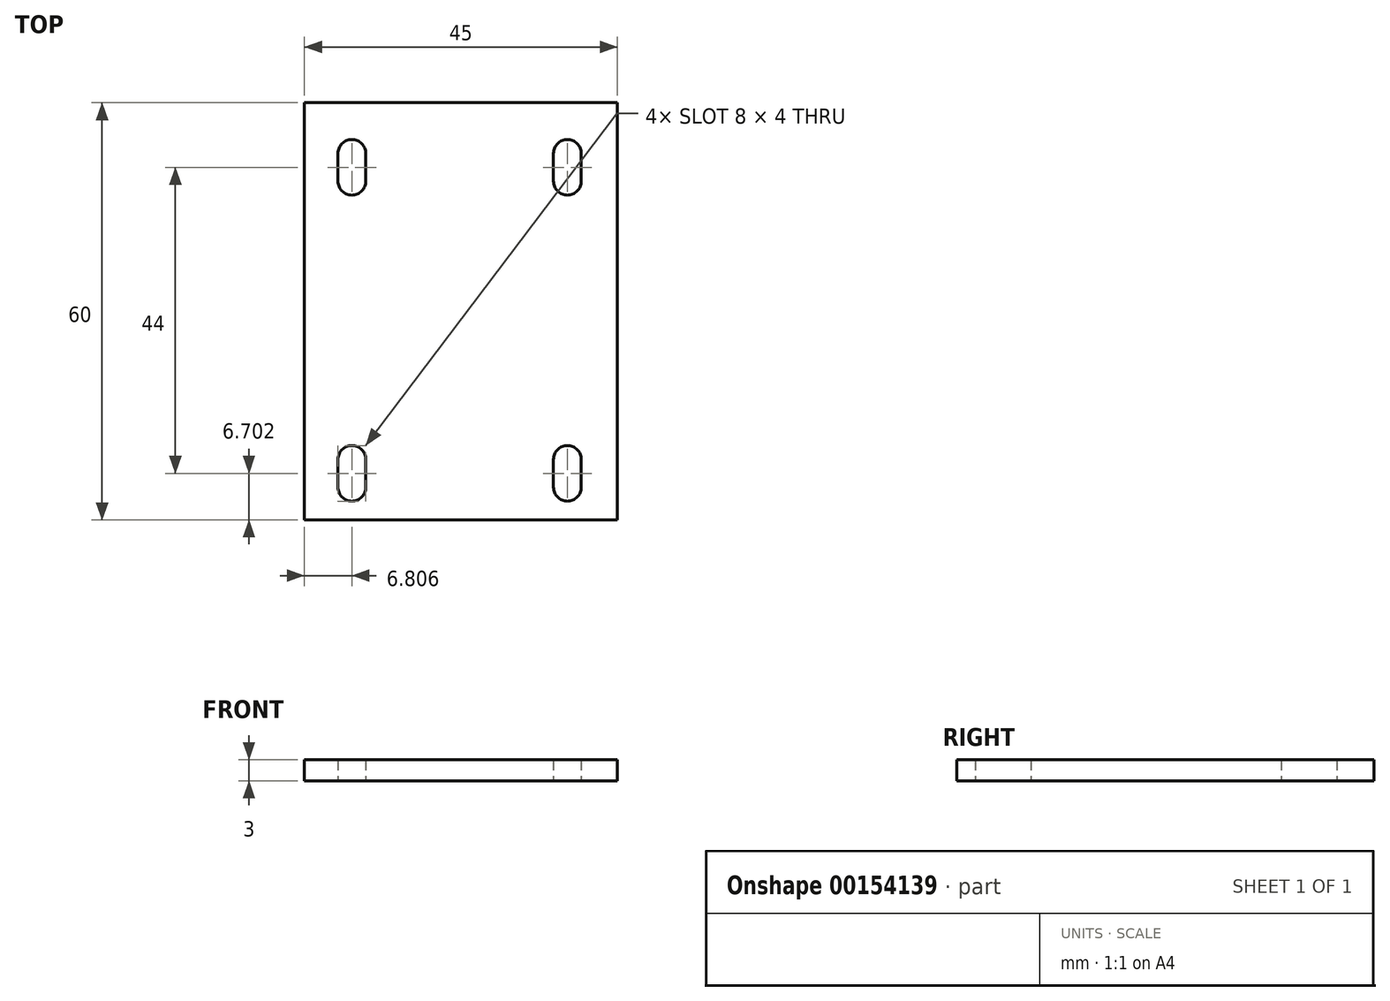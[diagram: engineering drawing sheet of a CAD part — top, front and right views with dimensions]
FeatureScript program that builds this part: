
annotation { "Feature Type Name" : "Feature", "Feature Type Description" : "" }
export const myFeature = defineFeature(function(context is Context, id is Id, definition is map)
    precondition{}
    {
        {
            var Q0;
            Q0=qCreatedBy(makeId("Top.planeOp"),FACE);
            var sketch = newSketch(context, id + "F0", { "sketchPlane" : qUnion([Q0])});
            skLineSegment(sketch, "E0.bottom", {"start": v(22.5, 30) * mm, "end": v(-22.5, 30) * mm});
            skLineSegment(sketch, "E0.top", {"start": v(22.5, -30) * mm, "end": v(-22.5, -30) * mm});
            skLineSegment(sketch, "E0.left", {"start": v(22.5, 30) * mm, "end": v(22.5, -30) * mm});
            skLineSegment(sketch, "E0.right", {"start": v(-22.5, 30) * mm, "end": v(-22.5, -30) * mm});
            skPoint(sketch, "E0.middle", {"position": v(0, 0) * mm});
            skLineSegment(sketch, "E1.bottom", {"start": v(-17.7, -25.3) * mm, "end": v(-13.7, -25.3) * mm});
            skLineSegment(sketch, "E1.top", {"start": v(-17.7, -21.3) * mm, "end": v(-13.7, -21.3) * mm});
            skLineSegment(sketch, "E1.left", {"start": v(-17.7, -25.3) * mm, "end": v(-17.7, -21.3) * mm});
            skLineSegment(sketch, "E1.right", {"start": v(-13.7, -25.3) * mm, "end": v(-13.7, -21.3) * mm});
            skArc(sketch, "E2", {"start": v(-17.7, -25.3) * mm, "mid": v(-15.7, -27.3) * mm, "end": v(-13.7, -25.3) * mm});
            skArc(sketch, "E3", {"start": v(-13.7, -21.3) * mm, "mid": v(-15.7, -19.3) * mm, "end": v(-17.7, -21.3) * mm});
            skLineSegment(sketch, "E4", {"start": v(-17.7, -21.3) * mm, "end": v(-13.7, -25.3) * mm});
            skLineSegment(sketch, "E5", {"start": v(-17.7, -25.3) * mm, "end": v(-13.7, -21.3) * mm});
            skPoint(sketch, "E6", {"position": v(-15.7, -23.3) * mm});
            skLineSegment(sketch, "E7.bottom", {"start": v(13.3, -25.3) * mm, "end": v(17.3, -25.3) * mm});
            skLineSegment(sketch, "E7.top", {"start": v(13.3, -21.3) * mm, "end": v(17.3, -21.3) * mm});
            skLineSegment(sketch, "E7.left", {"start": v(13.3, -25.3) * mm, "end": v(13.3, -21.3) * mm});
            skLineSegment(sketch, "E7.right", {"start": v(17.3, -25.3) * mm, "end": v(17.3, -21.3) * mm});
            skArc(sketch, "E8", {"start": v(13.3, -25.3) * mm, "mid": v(15.3, -27.3) * mm, "end": v(17.3, -25.3) * mm});
            skArc(sketch, "E9", {"start": v(17.3, -21.3) * mm, "mid": v(15.3, -19.3) * mm, "end": v(13.3, -21.3) * mm});
            skLineSegment(sketch, "E10", {"start": v(13.3, -21.3) * mm, "end": v(17.3, -25.3) * mm});
            skLineSegment(sketch, "E11", {"start": v(13.3, -25.3) * mm, "end": v(17.3, -21.3) * mm});
            skPoint(sketch, "E12", {"position": v(15.3, -23.3) * mm});
            skLineSegment(sketch, "E13.bottom", {"start": v(13.3, 18.7) * mm, "end": v(17.3, 18.7) * mm});
            skLineSegment(sketch, "E13.top", {"start": v(13.3, 22.7) * mm, "end": v(17.3, 22.7) * mm});
            skLineSegment(sketch, "E13.left", {"start": v(13.3, 18.7) * mm, "end": v(13.3, 22.7) * mm});
            skLineSegment(sketch, "E13.right", {"start": v(17.3, 18.7) * mm, "end": v(17.3, 22.7) * mm});
            skArc(sketch, "E14", {"start": v(13.3, 18.7) * mm, "mid": v(15.3, 16.7) * mm, "end": v(17.3, 18.7) * mm});
            skArc(sketch, "E15", {"start": v(17.3, 22.7) * mm, "mid": v(15.3, 24.7) * mm, "end": v(13.3, 22.7) * mm});
            skLineSegment(sketch, "E16", {"start": v(13.3, 22.7) * mm, "end": v(17.3, 18.7) * mm});
            skLineSegment(sketch, "E17", {"start": v(13.3, 18.7) * mm, "end": v(17.3, 22.7) * mm});
            skPoint(sketch, "E18", {"position": v(15.3, 20.7) * mm});
            skLineSegment(sketch, "E19.bottom", {"start": v(-17.7, 18.7) * mm, "end": v(-13.7, 18.7) * mm});
            skLineSegment(sketch, "E19.top", {"start": v(-17.7, 22.7) * mm, "end": v(-13.7, 22.7) * mm});
            skLineSegment(sketch, "E19.left", {"start": v(-17.7, 18.7) * mm, "end": v(-17.7, 22.7) * mm});
            skLineSegment(sketch, "E19.right", {"start": v(-13.7, 18.7) * mm, "end": v(-13.7, 22.7) * mm});
            skArc(sketch, "E20", {"start": v(-17.7, 18.7) * mm, "mid": v(-15.7, 16.7) * mm, "end": v(-13.7, 18.7) * mm});
            skArc(sketch, "E21", {"start": v(-13.7, 22.7) * mm, "mid": v(-15.7, 24.7) * mm, "end": v(-17.7, 22.7) * mm});
            skLineSegment(sketch, "E22", {"start": v(-17.7, 22.7) * mm, "end": v(-13.7, 18.7) * mm});
            skLineSegment(sketch, "E23", {"start": v(-17.7, 18.7) * mm, "end": v(-13.7, 22.7) * mm});
            skPoint(sketch, "E24", {"position": v(-15.7, 20.7) * mm});
            skLineSegment(sketch, "E25", {"start": v(-15.7, -23.3) * mm, "end": v(15.3, -23.3) * mm});
            skLineSegment(sketch, "E26", {"start": v(15.3, -23.3) * mm, "end": v(15.3, 20.7) * mm});
            skLineSegment(sketch, "E27", {"start": v(15.3, 20.7) * mm, "end": v(-15.7, 20.7) * mm});
            skLineSegment(sketch, "E28", {"start": v(-15.7, 20.7) * mm, "end": v(-15.7, -23.3) * mm});
            skSolve(sketch);
        }
        {
            var Q0;
            Q0 = qSketchRegion(id + "F0", true);
            var Q1;
            {var subQ0=sQuery(id+"F0.wireOp",EDGE,"E25");var subQ1=sQuery(id+"F0.wireOp",EDGE,"E1.right");var subQ2=makeQuery(id+"F0.imprint","INTERSECT",VERTEX,{"derivedFrom":[subQ1,subQ0]});Q1=makeQuery(id+"F0.imprint","IMPRINT",FACE,{"disambiguationData":[TD([[makeQuery(id+"F0.imprint","IMPRINT",EDGE,{"disambiguationData":[TD([[subQ2,-1.0]])],"derivedFrom":subQ0}),1.0]])]});}
            extrude(context, id + "F1", {"entities" : qUnion([Q0, Q1]), "depth" : 3 * mm});
        }
    });
